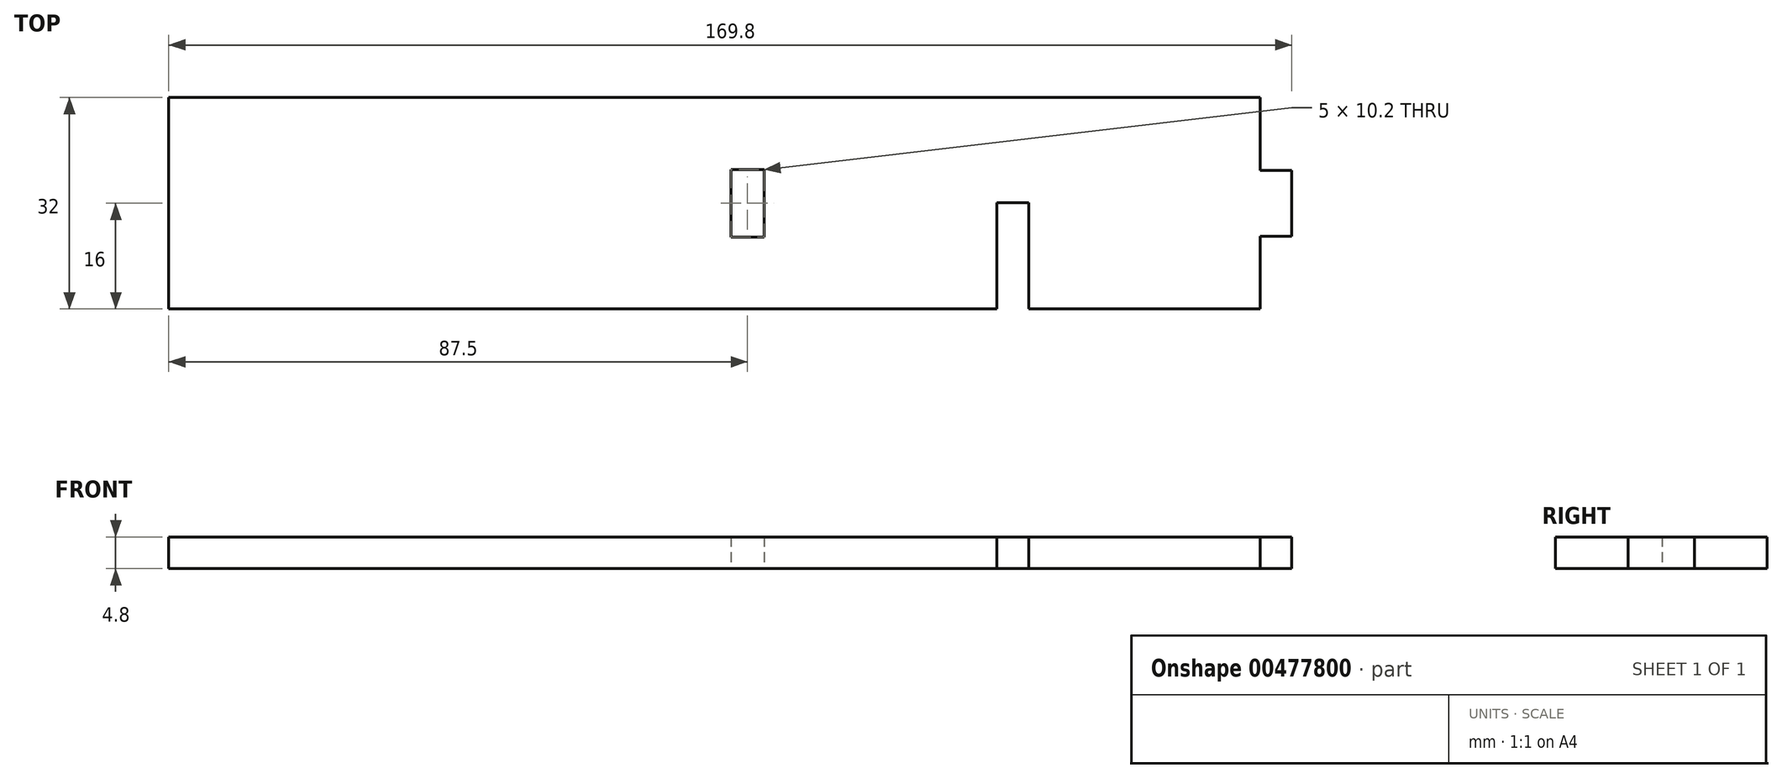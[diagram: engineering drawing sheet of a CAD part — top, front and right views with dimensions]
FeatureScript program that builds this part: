
annotation { "Feature Type Name" : "Feature", "Feature Type Description" : "" }
export const myFeature = defineFeature(function(context is Context, id is Id, definition is map)
    precondition{}
    {
        {
            var Q0;
            Q0=qCreatedBy(makeId("Top.planeOp"),FACE);
            var sketch = newSketch(context, id + "F0", { "sketchPlane" : qUnion([Q0])});
            skLineSegment(sketch, "E0.bottom", {"start": v(0, 0) * mm, "end": v(165, 0) * mm});
            skLineSegment(sketch, "E0.top", {"start": v(0, 32) * mm, "end": v(165, 32) * mm});
            skLineSegment(sketch, "E0.left", {"start": v(0, 0) * mm, "end": v(0, 32) * mm});
            skLineSegment(sketch, "E0.right", {"start": v(165, 0) * mm, "end": v(165, 32) * mm});
            skLineSegment(sketch, "E1.bottom", {"start": v(165, 21) * mm, "end": v(169.8, 21) * mm});
            skLineSegment(sketch, "E1.top", {"start": v(165, 11) * mm, "end": v(169.8, 11) * mm});
            skLineSegment(sketch, "E1.left", {"start": v(165, 21) * mm, "end": v(165, 11) * mm});
            skLineSegment(sketch, "E1.right", {"start": v(169.8, 21) * mm, "end": v(169.8, 11) * mm});
            skLineSegment(sketch, "E2.bottom", {"start": v(125.2, 0) * mm, "end": v(130, 0) * mm});
            skLineSegment(sketch, "E2.top", {"start": v(125.2, 16.1) * mm, "end": v(130, 16.1) * mm});
            skLineSegment(sketch, "E2.left", {"start": v(125.2, 0) * mm, "end": v(125.2, 16.1) * mm});
            skLineSegment(sketch, "E2.right", {"start": v(130, 0) * mm, "end": v(130, 16.1) * mm});
            skLineSegment(sketch, "E3.bottom", {"start": v(85, 21.1) * mm, "end": v(90, 21.1) * mm});
            skLineSegment(sketch, "E3.top", {"start": v(85, 10.9) * mm, "end": v(90, 10.9) * mm});
            skLineSegment(sketch, "E3.left", {"start": v(85, 21.1) * mm, "end": v(85, 10.9) * mm});
            skLineSegment(sketch, "E3.right", {"start": v(90, 21.1) * mm, "end": v(90, 10.9) * mm});
            skSolve(sketch);
        }
        {
            var Q0;
            {var subQ2=sQuery(id+"F0.wireOp",EDGE,"E0.top");Q0=makeQuery(id+"F0.imprint","IMPRINT",FACE,{"disambiguationData":[TD([[makeQuery(id+"F0.imprint","IMPRINT",EDGE,{"derivedFrom":subQ2}),-1.0]])]});}
            var Q1;
            Q1=makeQuery(id+"F0.imprint","IMPRINT",FACE,{"disambiguationData":[TD([[makeQuery(id+"F0.imprint","IMPRINT",EDGE,{"derivedFrom":sQuery(id+"F0.wireOp",EDGE,"E1.bottom")}),-1.0]])]});
            extrude(context, id + "F1", {"entities" : qUnion([Q0, Q1]), "depth" : 4.8 * mm});
        }
    });
